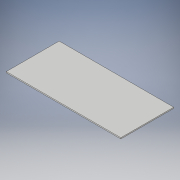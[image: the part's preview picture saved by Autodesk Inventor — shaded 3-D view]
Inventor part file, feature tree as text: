
AUTODESK INVENTOR PART (.ipt)
format: ipt  version: 2017 (Build 210142000, 142)  size: 89,600 bytes
history: native  units: in
note: dims shown in document units (in); Inventor stores cm internally (conversion verified against a paired STEP export)
features: extrude x1, sketch x1
ambient origin geometry x8: Origin, YZ Plane, XZ Plane, XY Plane, X Axis, Y Axis, Z Axis, Center Point
bodies: Solid1 (feature_tree)
feature tree (2):
  extrude  "Extrusion1"  Depth=6.0in
  sketch  "Sketch1"  dims[d0=13.0in d1=6.0in d2=0.125in d3=0.0in]
